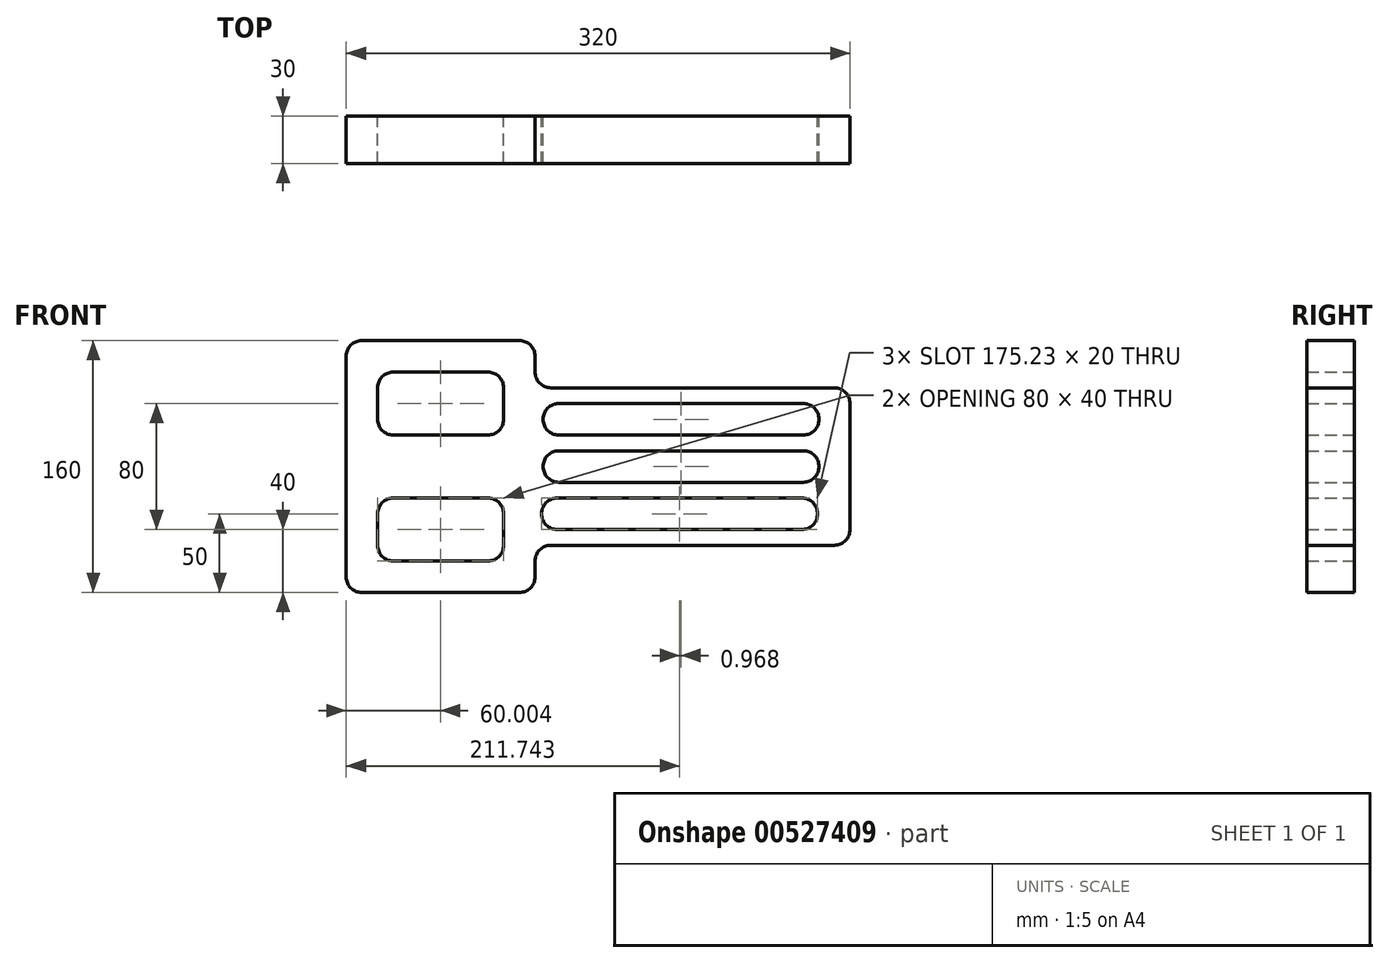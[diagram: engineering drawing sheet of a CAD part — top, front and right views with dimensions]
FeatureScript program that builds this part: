
annotation { "Feature Type Name" : "Feature", "Feature Type Description" : "" }
export const myFeature = defineFeature(function(context is Context, id is Id, definition is map)
    precondition{}
    {
        {
            var Q0;
            Q0=qCreatedBy(makeId("Front.planeOp"),FACE);
            var sketch = newSketch(context, id + "F0", { "sketchPlane" : qUnion([Q0])});
            skLineSegment(sketch, "E0", {"start": v(211.12, 80) * mm, "end": v(211.12, 0) * mm});
            skLineSegment(sketch, "E1", {"start": v(201.12, -10) * mm, "end": v(21.12, -10) * mm});
            skLineSegment(sketch, "E2", {"start": v(11.12, -20) * mm, "end": v(11.12, -30) * mm});
            skLineSegment(sketch, "E3", {"start": v(1.12, -40) * mm, "end": v(-98.88, -40) * mm});
            skLineSegment(sketch, "E4", {"start": v(-108.88, -30) * mm, "end": v(-108.88, 110) * mm});
            skLineSegment(sketch, "E5", {"start": v(-98.88, 120) * mm, "end": v(1.12, 120) * mm});
            skLineSegment(sketch, "E6", {"start": v(11.12, 110) * mm, "end": v(11.12, 100) * mm});
            skLineSegment(sketch, "E7", {"start": v(21.12, 90) * mm, "end": v(201.12, 90) * mm});
            skPoint(sketch, "E8.visualSharp", {"position": v(11.12, 90) * mm});
            skArc(sketch, "E8.filletArc", {"start": v(11.12, 100) * mm, "mid": v(14.05, 92.93) * mm, "end": v(21.12, 90) * mm});
            skPoint(sketch, "E9.visualSharp", {"position": v(11.12, -10) * mm});
            skArc(sketch, "E9.filletArc", {"start": v(21.12, -10) * mm, "mid": v(14.05, -12.93) * mm, "end": v(11.12, -20) * mm});
            skPoint(sketch, "E10.visualSharp", {"position": v(-108.88, 120) * mm});
            skArc(sketch, "E10.filletArc", {"start": v(-98.88, 120) * mm, "mid": v(-105.95, 117.07) * mm, "end": v(-108.88, 110) * mm});
            skPoint(sketch, "E11.visualSharp", {"position": v(-108.88, -40) * mm});
            skArc(sketch, "E11.filletArc", {"start": v(-108.88, -30) * mm, "mid": v(-105.95, -37.07) * mm, "end": v(-98.88, -40) * mm});
            skPoint(sketch, "E12.visualSharp", {"position": v(11.12, 120) * mm});
            skArc(sketch, "E12.filletArc", {"start": v(11.12, 110) * mm, "mid": v(8.2, 117.07) * mm, "end": v(1.12, 120) * mm});
            skPoint(sketch, "E13.start.orphan", {"position": v(-108.88, 40) * mm});
            skLineSegment(sketch, "E14.bottom", {"start": v(-78.88, 100) * mm, "end": v(-18.88, 100) * mm});
            skLineSegment(sketch, "E14.top", {"start": v(-78.88, 60) * mm, "end": v(-18.88, 60) * mm});
            skLineSegment(sketch, "E14.left", {"start": v(-88.88, 90) * mm, "end": v(-88.88, 70) * mm});
            skLineSegment(sketch, "E14.right", {"start": v(-8.88, 90) * mm, "end": v(-8.88, 70) * mm});
            skLineSegment(sketch, "E15.bottom", {"start": v(-78.88, 20) * mm, "end": v(-18.88, 20) * mm});
            skLineSegment(sketch, "E15.top", {"start": v(-78.88, -20) * mm, "end": v(-18.88, -20) * mm});
            skLineSegment(sketch, "E15.left", {"start": v(-88.88, 10) * mm, "end": v(-88.88, -10) * mm});
            skLineSegment(sketch, "E15.right", {"start": v(-8.88, 10) * mm, "end": v(-8.88, -10) * mm});
            skLineSegment(sketch, "E16.bottom", {"start": v(26.21, 50) * mm, "end": v(181.45, 50) * mm});
            skLineSegment(sketch, "E16.top", {"start": v(26.21, 30) * mm, "end": v(181.45, 30) * mm});
            skLineSegment(sketch, "E16.left", {"start": v(16.21, 40) * mm, "end": v(16.21, 40) * mm});
            skLineSegment(sketch, "E16.right", {"start": v(191.45, 40) * mm, "end": v(191.45, 40) * mm});
            skLineSegment(sketch, "E17.bottom", {"start": v(26.21, 80) * mm, "end": v(181.45, 80) * mm});
            skLineSegment(sketch, "E17.top", {"start": v(26.21, 60) * mm, "end": v(181.45, 60) * mm});
            skLineSegment(sketch, "E17.left", {"start": v(16.21, 70) * mm, "end": v(16.21, 70) * mm});
            skLineSegment(sketch, "E17.right", {"start": v(191.45, 70) * mm, "end": v(191.45, 70) * mm});
            skLineSegment(sketch, "E18.bottom", {"start": v(25.25, 20) * mm, "end": v(180.48, 20) * mm});
            skLineSegment(sketch, "E18.top", {"start": v(25.25, 0) * mm, "end": v(180.48, 0) * mm});
            skLineSegment(sketch, "E18.left", {"start": v(15.25, 10) * mm, "end": v(15.25, 10) * mm});
            skLineSegment(sketch, "E18.right", {"start": v(190.48, 10) * mm, "end": v(190.48, 10) * mm});
            skPoint(sketch, "E19.visualSharp", {"position": v(211.12, 90) * mm});
            skArc(sketch, "E19.filletArc", {"start": v(211.12, 80) * mm, "mid": v(208.2, 87.07) * mm, "end": v(201.12, 90) * mm});
            skPoint(sketch, "E20.visualSharp", {"position": v(211.12, -10) * mm});
            skArc(sketch, "E20.filletArc", {"start": v(201.12, -10) * mm, "mid": v(208.2, -7.07) * mm, "end": v(211.12, 0) * mm});
            skPoint(sketch, "E21.visualSharp", {"position": v(16.21, 80) * mm});
            skArc(sketch, "E21.filletArc", {"start": v(26.21, 80) * mm, "mid": v(19.14, 77.07) * mm, "end": v(16.21, 70) * mm});
            skPoint(sketch, "E22.visualSharp", {"position": v(16.21, 60) * mm});
            skArc(sketch, "E22.filletArc", {"start": v(16.21, 70) * mm, "mid": v(19.14, 62.93) * mm, "end": v(26.21, 60) * mm});
            skPoint(sketch, "E23.visualSharp", {"position": v(16.21, 50) * mm});
            skArc(sketch, "E23.filletArc", {"start": v(26.21, 50) * mm, "mid": v(19.14, 47.07) * mm, "end": v(16.21, 40) * mm});
            skPoint(sketch, "E24.visualSharp", {"position": v(16.21, 30) * mm});
            skArc(sketch, "E24.filletArc", {"start": v(16.21, 40) * mm, "mid": v(19.14, 32.93) * mm, "end": v(26.21, 30) * mm});
            skPoint(sketch, "E25.visualSharp", {"position": v(15.25, 20) * mm});
            skArc(sketch, "E25.filletArc", {"start": v(25.25, 20) * mm, "mid": v(18.18, 17.07) * mm, "end": v(15.25, 10) * mm});
            skPoint(sketch, "E26.visualSharp", {"position": v(15.25, 0) * mm});
            skArc(sketch, "E26.filletArc", {"start": v(15.25, 10) * mm, "mid": v(18.18, 2.93) * mm, "end": v(25.25, 0) * mm});
            skPoint(sketch, "E27.visualSharp", {"position": v(-8.88, 20) * mm});
            skArc(sketch, "E27.filletArc", {"start": v(-8.88, 10) * mm, "mid": v(-11.8, 17.07) * mm, "end": v(-18.88, 20) * mm});
            skPoint(sketch, "E28.visualSharp", {"position": v(-88.88, 20) * mm});
            skArc(sketch, "E28.filletArc", {"start": v(-78.88, 20) * mm, "mid": v(-85.95, 17.07) * mm, "end": v(-88.88, 10) * mm});
            skPoint(sketch, "E29.visualSharp", {"position": v(-88.88, -20) * mm});
            skArc(sketch, "E29.filletArc", {"start": v(-88.88, -10) * mm, "mid": v(-85.95, -17.07) * mm, "end": v(-78.88, -20) * mm});
            skPoint(sketch, "E30.visualSharp", {"position": v(-8.88, -20) * mm});
            skArc(sketch, "E30.filletArc", {"start": v(-18.88, -20) * mm, "mid": v(-11.8, -17.07) * mm, "end": v(-8.88, -10) * mm});
            skPoint(sketch, "E31.visualSharp", {"position": v(11.12, -40) * mm});
            skArc(sketch, "E31.filletArc", {"start": v(1.12, -40) * mm, "mid": v(8.2, -37.07) * mm, "end": v(11.12, -30) * mm});
            skPoint(sketch, "E32.visualSharp", {"position": v(-8.88, 60) * mm});
            skArc(sketch, "E32.filletArc", {"start": v(-18.88, 60) * mm, "mid": v(-11.8, 62.93) * mm, "end": v(-8.88, 70) * mm});
            skPoint(sketch, "E33.visualSharp", {"position": v(-88.88, 100) * mm});
            skArc(sketch, "E33.filletArc", {"start": v(-78.88, 100) * mm, "mid": v(-85.95, 97.07) * mm, "end": v(-88.88, 90) * mm});
            skPoint(sketch, "E34.visualSharp", {"position": v(-88.88, 60) * mm});
            skArc(sketch, "E34.filletArc", {"start": v(-88.88, 70) * mm, "mid": v(-85.95, 62.93) * mm, "end": v(-78.88, 60) * mm});
            skPoint(sketch, "E35.visualSharp", {"position": v(-8.88, 100) * mm});
            skArc(sketch, "E35.filletArc", {"start": v(-8.88, 90) * mm, "mid": v(-11.8, 97.07) * mm, "end": v(-18.88, 100) * mm});
            skPoint(sketch, "E36.visualSharp", {"position": v(191.45, 80) * mm});
            skArc(sketch, "E36.filletArc", {"start": v(191.45, 70) * mm, "mid": v(188.52, 77.07) * mm, "end": v(181.45, 80) * mm});
            skPoint(sketch, "E37.visualSharp", {"position": v(191.45, 50) * mm});
            skArc(sketch, "E37.filletArc", {"start": v(191.45, 40) * mm, "mid": v(188.52, 47.07) * mm, "end": v(181.45, 50) * mm});
            skPoint(sketch, "E38.visualSharp", {"position": v(190.48, 20) * mm});
            skArc(sketch, "E38.filletArc", {"start": v(190.48, 10) * mm, "mid": v(187.55, 17.07) * mm, "end": v(180.48, 20) * mm});
            skPoint(sketch, "E39.visualSharp", {"position": v(190.48, 0) * mm});
            skArc(sketch, "E39.filletArc", {"start": v(180.48, 0) * mm, "mid": v(187.55, 2.93) * mm, "end": v(190.48, 10) * mm});
            skPoint(sketch, "E40.visualSharp", {"position": v(191.45, 30) * mm});
            skArc(sketch, "E40.filletArc", {"start": v(181.45, 30) * mm, "mid": v(188.52, 32.93) * mm, "end": v(191.45, 40) * mm});
            skPoint(sketch, "E41.visualSharp", {"position": v(191.45, 60) * mm});
            skArc(sketch, "E41.filletArc", {"start": v(181.45, 60) * mm, "mid": v(188.52, 62.93) * mm, "end": v(191.45, 70) * mm});
            skSolve(sketch);
        }
        {
            var Q0;
            Q0=makeQuery(id+"F0.imprint","IMPRINT",FACE,{"disambiguationData":[TD([[makeQuery(id+"F0.imprint","IMPRINT",EDGE,{"derivedFrom":sQuery(id+"F0.wireOp",EDGE,"E0")}),-1.0]])]});
            extrude(context, id + "F1", {"entities" : qUnion([Q0]), "depth" : 30 * mm, "offsetDistance" : 25 * mm});
        }
    });
